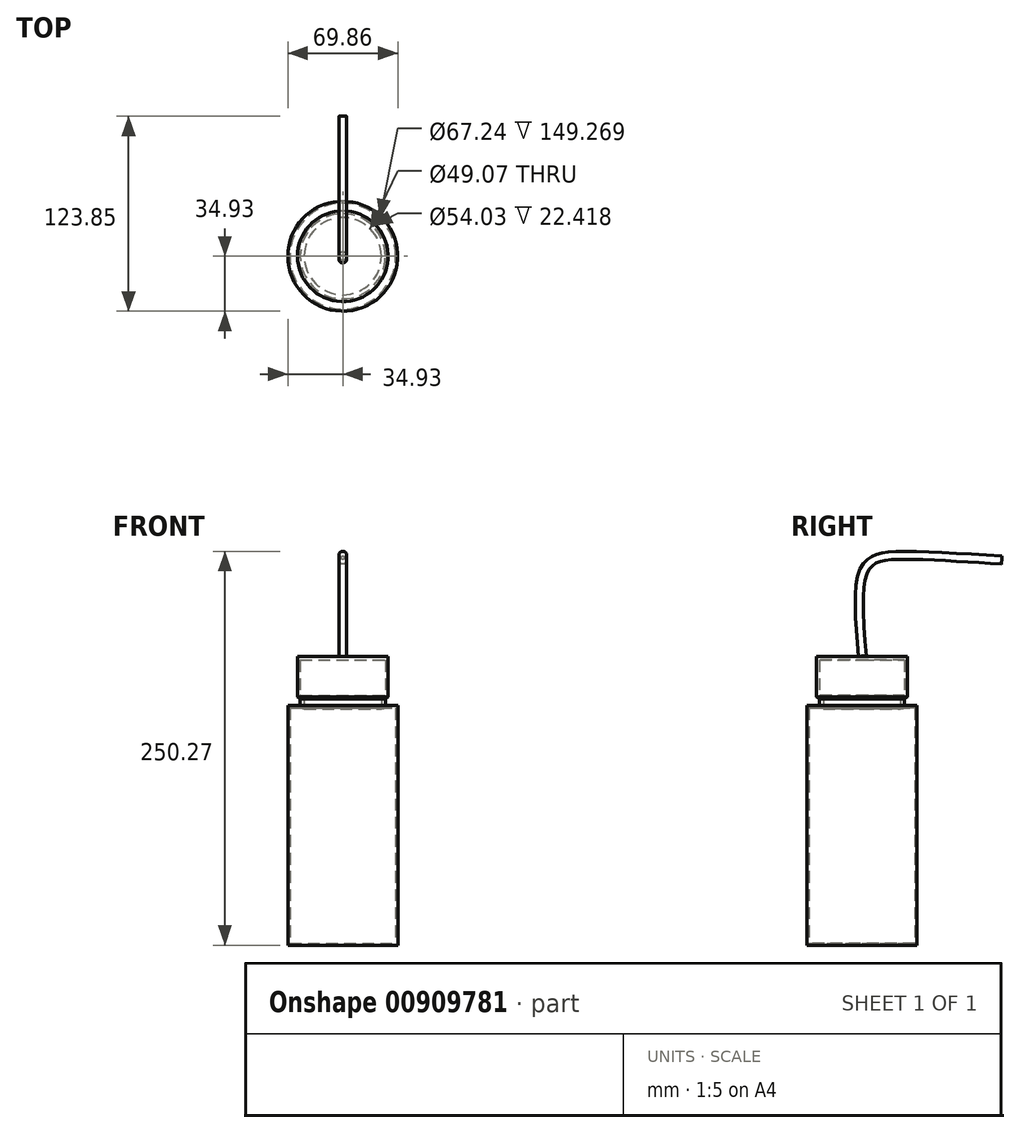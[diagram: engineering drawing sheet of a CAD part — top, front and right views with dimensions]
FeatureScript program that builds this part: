
annotation { "Feature Type Name" : "Feature", "Feature Type Description" : "" }
export const myFeature = defineFeature(function(context is Context, id is Id, definition is map)
    precondition{}
    {
        {
            var Q0;
            Q0=qCreatedBy(makeId("Front.planeOp"),FACE);
            var sketch = newSketch(context, id + "F0", { "sketchPlane" : qUnion([Q0])});
            skLineSegment(sketch, "E0", {"start": v(0, 0) * mm, "end": v(0, 152.4) * mm, "construction": true});
            skLineSegment(sketch, "E1", {"start": v(0, 0) * mm, "end": v(-34.93, 0) * mm});
            skLineSegment(sketch, "E2", {"start": v(0, 1.34) * mm, "end": v(-33.62, 1.34) * mm});
            skLineSegment(sketch, "E3", {"start": v(-33.62, 1.34) * mm, "end": v(-33.62, 150.61) * mm});
            skLineSegment(sketch, "E4", {"start": v(-34.93, 0) * mm, "end": v(-34.93, 152.4) * mm});
            skLineSegment(sketch, "E5", {"start": v(-34.93, 152.4) * mm, "end": v(-30.01, 152.4) * mm});
            skLineSegment(sketch, "E6", {"start": v(-33.62, 150.61) * mm, "end": v(-28.2, 150.61) * mm});
            skLineSegment(sketch, "E7", {"start": v(0, 1.34) * mm, "end": v(0, 0) * mm});
            skLineSegment(sketch, "E8", {"start": v(-30.01, 152.4) * mm, "end": v(-27.02, 152.4) * mm});
            skLineSegment(sketch, "E9", {"start": v(-27.02, 152.4) * mm, "end": v(-27.02, 156.42) * mm});
            skLineSegment(sketch, "E10", {"start": v(-27.02, 156.42) * mm, "end": v(-28.81, 157.7) * mm});
            skLineSegment(sketch, "E11", {"start": v(-28.81, 157.7) * mm, "end": v(-28.81, 183.38) * mm});
            skLineSegment(sketch, "E12", {"start": v(-28.81, 183.38) * mm, "end": v(0, 183.38) * mm});
            skLineSegment(sketch, "E13", {"start": v(0, 183.38) * mm, "end": v(0, 181.15) * mm});
            skLineSegment(sketch, "E14", {"start": v(0, 181.15) * mm, "end": v(-27.02, 181.15) * mm});
            skLineSegment(sketch, "E15", {"start": v(-27.02, 181.15) * mm, "end": v(-27.02, 158.73) * mm});
            skLineSegment(sketch, "E16", {"start": v(-27.02, 158.73) * mm, "end": v(-24.53, 156.42) * mm});
            skLineSegment(sketch, "E17", {"start": v(-24.53, 156.42) * mm, "end": v(-24.53, 150.18) * mm});
            skLineSegment(sketch, "E18", {"start": v(-24.53, 150.18) * mm, "end": v(-28.2, 150.61) * mm});
            skLineSegment(sketch, "E19", {"start": v(0, 152.4) * mm, "end": v(0, 183.38) * mm, "construction": true});
            skSolve(sketch);
        }
        {
            var Q0;
            Q0 = qSketchRegion(id + "F0", true);
            var Q1;
            Q1=sQuery(id+"F0.wireOp",EDGE,"E19");
            revolve(context, id + "F1", {"surfaceOperationType" : NewSurfaceOperationType.NEW, "entities" : qUnion([Q0]), "axis" : qUnion([Q1]), "revolveType" : RevolveType.FULL});
        }
        {
            var Q0;
            Q0=qCreatedBy(makeId("Right.planeOp"),FACE);
            var sketch = newSketch(context, id + "F2", { "sketchPlane" : qUnion([Q0])});
            skLineSegment(sketch, "E20", {"start": v(-28.89, 183.67) * mm, "end": v(28.22, 183.67) * mm});
            skLineSegment(sketch, "E21", {"start": v(-28.89, 183.67) * mm, "end": v(0, 183.67) * mm});
            skFitSpline(sketch, "E22", {"points": [v(0, 183.67) * mm, v(0, 235.46) * mm, v(7.15, 244.8) * mm, v(18.81, 247.71) * mm, v(88.77, 244.8) * mm], "startDerivative": vector(-15.43, 193.64) * mm, "endDerivative": vector(227, -15.14) * mm});
            skSolve(sketch);
        }
        {
            var Q0;
            Q0=sQuery(id+"F2.wireOp",EDGE,"E22");
            var Q1;
            Q1=sQuery(id+"F2.wireOp",VERTEX,"E22.end");
            cPlane(context, id + "F3", {"entities" : qUnion([Q0, Q1]), "cplaneType" : CPlaneType.CURVE_POINT, "offset" : 25.4 * mm, "width" : 152.4 * mm, "height" : 152.4 * mm});
        }
        {
            var Q0;
            Q0=qCreatedBy(id+"F3.planeOp",FACE);
            var sketch = newSketch(context, id + "F4", { "sketchPlane" : qUnion([Q0])});
            skCircle(sketch, "E23", {"center": v(0, 249.98) * mm, "radius": 2.53 * mm});
            skSolve(sketch);
        }
        {
            var Q0;
            Q0=makeQuery(id+"F4.imprint","IMPRINT",FACE,{"disambiguationData":[TD([[makeQuery(id+"F4.imprint","IMPRINT",EDGE,{"derivedFrom":sQuery(id+"F4.wireOp",EDGE,"E23")}),1.0]])]});
            var Q1;
            Q1=sQuery(id+"F2.wireOp",EDGE,"E22");
            sweep(context, id + "F5", {"profiles" : qUnion([Q0]), "path" : qUnion([Q1])});
        }
    });
